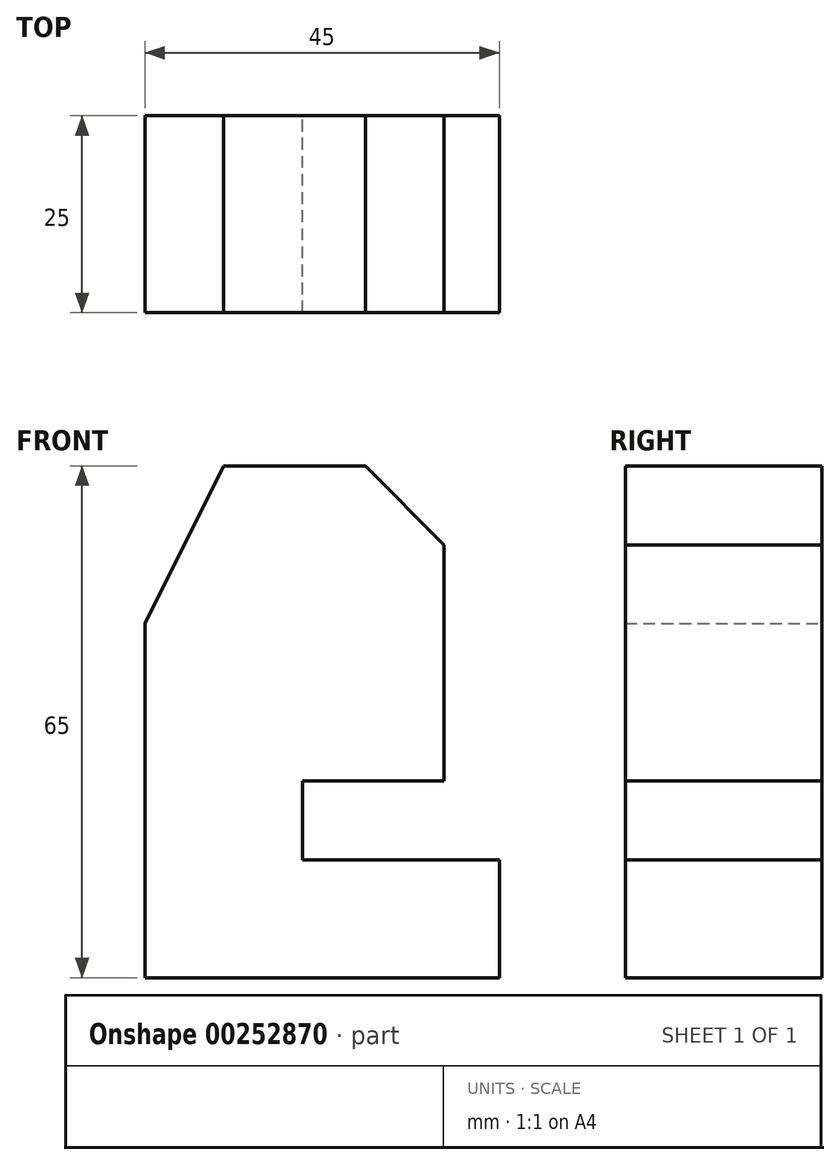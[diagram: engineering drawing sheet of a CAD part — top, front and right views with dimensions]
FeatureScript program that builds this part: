
annotation { "Feature Type Name" : "Feature", "Feature Type Description" : "" }
export const myFeature = defineFeature(function(context is Context, id is Id, definition is map)
    precondition{}
    {
        {
            var Q0;
            Q0=qCreatedBy(makeId("Front.planeOp"),FACE);
            var sketch = newSketch(context, id + "F0", { "sketchPlane" : qUnion([Q0])});
            skLineSegment(sketch, "E0", {"start": v(0, 0) * mm, "end": v(0, 45) * mm});
            skLineSegment(sketch, "E1", {"start": v(0, 45) * mm, "end": v(10, 65) * mm});
            skLineSegment(sketch, "E2", {"start": v(10, 65) * mm, "end": v(28, 65) * mm});
            skLineSegment(sketch, "E3", {"start": v(28, 65) * mm, "end": v(38, 55) * mm});
            skLineSegment(sketch, "E4", {"start": v(38, 55) * mm, "end": v(38, 25) * mm});
            skLineSegment(sketch, "E5", {"start": v(38, 25) * mm, "end": v(20, 25) * mm});
            skLineSegment(sketch, "E6", {"start": v(20, 25) * mm, "end": v(20, 15) * mm});
            skLineSegment(sketch, "E7", {"start": v(20, 15) * mm, "end": v(45, 15) * mm});
            skLineSegment(sketch, "E8", {"start": v(45, 15) * mm, "end": v(45, 0) * mm});
            skLineSegment(sketch, "E9", {"start": v(45, 0) * mm, "end": v(0, 0) * mm});
            skSolve(sketch);
        }
        {
            var Q0;
            Q0=makeQuery(id+"F0.imprint","IMPRINT",FACE,{"disambiguationData":[TD([[makeQuery(id+"F0.imprint","IMPRINT",EDGE,{"derivedFrom":sQuery(id+"F0.wireOp",EDGE,"E0")}),-1.0]])]});
            extrude(context, id + "F1", {"entities" : qUnion([Q0]), "depth" : 25 * mm, "symmetric" : true});
        }
    });
